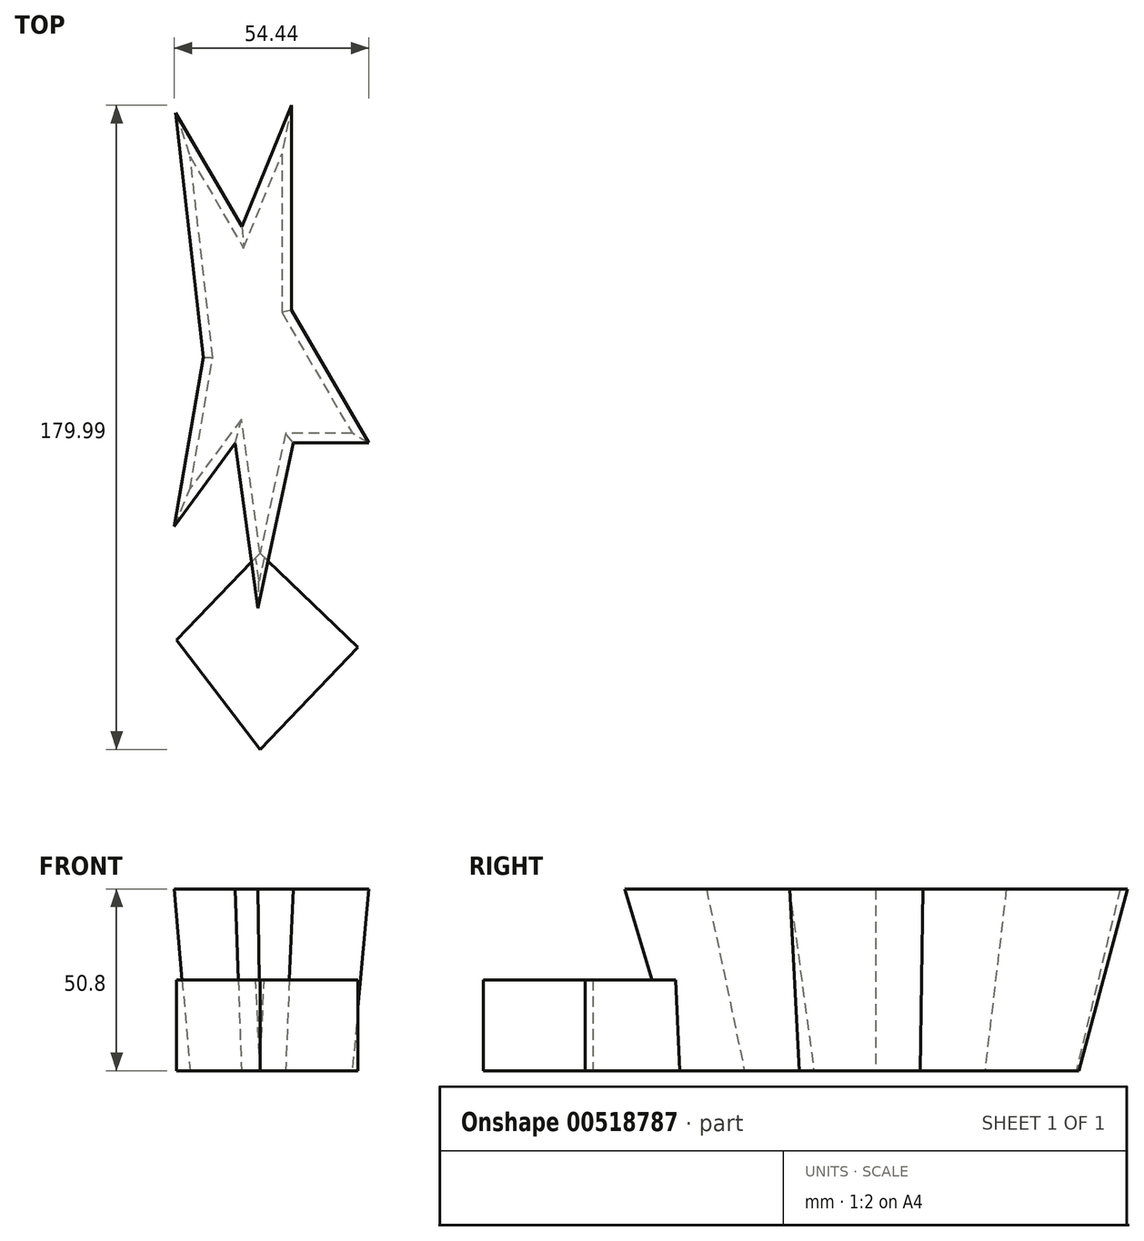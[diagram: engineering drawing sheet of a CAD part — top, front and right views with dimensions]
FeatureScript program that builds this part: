
annotation { "Feature Type Name" : "Feature", "Feature Type Description" : "" }
export const myFeature = defineFeature(function(context is Context, id is Id, definition is map)
    precondition{}
    {
        {
            var Q0;
            Q0=qCreatedBy(makeId("Top.planeOp"),FACE);
            var sketch = newSketch(context, id + "F0", { "sketchPlane" : qUnion([Q0])});
            skLineSegment(sketch, "E0", {"start": v(0, 0) * mm, "end": v(7.14, 33.47) * mm});
            skLineSegment(sketch, "E1", {"start": v(7.14, 33.47) * mm, "end": v(25.78, 33.47) * mm});
            skLineSegment(sketch, "E2", {"start": v(25.78, 33.47) * mm, "end": v(6.1, 67.24) * mm});
            skLineSegment(sketch, "E3", {"start": v(6.1, 67.24) * mm, "end": v(6.1, 111.57) * mm});
            skLineSegment(sketch, "E4", {"start": v(6.1, 111.57) * mm, "end": v(-4.61, 85.27) * mm});
            skLineSegment(sketch, "E5", {"start": v(-4.61, 85.27) * mm, "end": v(-19.5, 110.8) * mm});
            skLineSegment(sketch, "E6", {"start": v(-19.5, 110.8) * mm, "end": v(-13.2, 54.71) * mm});
            skLineSegment(sketch, "E7", {"start": v(-13.2, 54.71) * mm, "end": v(-19.5, 18.1) * mm});
            skLineSegment(sketch, "E8", {"start": v(-19.5, 18.1) * mm, "end": v(-5.2, 37.52) * mm});
            skLineSegment(sketch, "E9", {"start": v(-5.2, 37.52) * mm, "end": v(0, 0) * mm});
            skSolve(sketch);
        }
        {
            var Q0;
            Q0=makeQuery(id+"F0.imprint","IMPRINT",FACE,{"disambiguationData":[TD([[makeQuery(id+"F0.imprint","IMPRINT",EDGE,{"derivedFrom":sQuery(id+"F0.wireOp",EDGE,"E0")}),1.0]])]});
            extrude(context, id + "F1", {"entities" : qUnion([Q0]), "depth" : 50.8 * mm, "hasDraft" : true, "draftAngle" : 3 * degree});
        }
        {
            var Q0;
            Q0=qCreatedBy(makeId("Top.planeOp"),FACE);
            var sketch = newSketch(context, id + "F2", { "sketchPlane" : qUnion([Q0])});
            skLineSegment(sketch, "E10", {"start": v(0, 0) * mm, "end": v(27.38, -26.36) * mm});
            skLineSegment(sketch, "E11", {"start": v(27.38, -26.36) * mm, "end": v(0, -54.8) * mm});
            skLineSegment(sketch, "E12", {"start": v(0, -54.8) * mm, "end": v(50.11, -40.89) * mm});
            skLineSegment(sketch, "E13", {"start": v(50.11, -40.89) * mm, "end": v(40.59, -71) * mm});
            skLineSegment(sketch, "E14", {"start": v(40.59, -71) * mm, "end": v(82.99, -35.73) * mm});
            skLineSegment(sketch, "E15", {"start": v(82.99, -35.73) * mm, "end": v(117.82, -22.02) * mm});
            skLineSegment(sketch, "E16", {"start": v(117.82, -22.02) * mm, "end": v(97.28, 5.14) * mm});
            skLineSegment(sketch, "E17", {"start": v(97.28, 5.14) * mm, "end": v(106.73, 35) * mm});
            skLineSegment(sketch, "E18", {"start": v(106.73, 35) * mm, "end": v(67.32, 5.14) * mm});
            skLineSegment(sketch, "E19", {"start": v(67.32, 5.14) * mm, "end": v(57.62, 39.05) * mm});
            skLineSegment(sketch, "E20", {"start": v(57.62, 39.05) * mm, "end": v(45.27, 0) * mm});
            skLineSegment(sketch, "E21", {"start": v(45.27, 0) * mm, "end": v(0, 0) * mm});
            skLineSegment(sketch, "E22", {"start": v(0, 0) * mm, "end": v(-23.35, -24.26) * mm});
            skLineSegment(sketch, "E23", {"start": v(-23.35, -24.26) * mm, "end": v(0, -54.8) * mm});
            skLineSegment(sketch, "E24", {"start": v(0, -54.8) * mm, "end": v(-29.74, -54.8) * mm});
            skLineSegment(sketch, "E25", {"start": v(-29.74, -54.8) * mm, "end": v(-29.74, -76.29) * mm});
            skLineSegment(sketch, "E26", {"start": v(-29.74, -76.29) * mm, "end": v(-47.93, -58.78) * mm});
            skLineSegment(sketch, "E27", {"start": v(-47.93, -58.78) * mm, "end": v(-73.23, -71) * mm});
            skLineSegment(sketch, "E28", {"start": v(-73.23, -71) * mm, "end": v(-57.23, -51.4) * mm});
            skLineSegment(sketch, "E29", {"start": v(-57.23, -51.4) * mm, "end": v(-82.46, -51.4) * mm});
            skLineSegment(sketch, "E30", {"start": v(-82.46, -51.4) * mm, "end": v(-61.8, -35.73) * mm});
            skLineSegment(sketch, "E31", {"start": v(-61.8, -35.73) * mm, "end": v(-67.46, -15.9) * mm});
            skLineSegment(sketch, "E32", {"start": v(-67.46, -15.9) * mm, "end": v(-46.86, -35.73) * mm});
            skLineSegment(sketch, "E33", {"start": v(-46.86, -35.73) * mm, "end": v(-34.43, -6.34) * mm});
            skLineSegment(sketch, "E34", {"start": v(-34.43, -6.34) * mm, "end": v(-34.43, -35.73) * mm});
            skLineSegment(sketch, "E35", {"start": v(-34.43, -35.73) * mm, "end": v(0, -54.8) * mm});
            skSolve(sketch);
        }
        {
            var Q0;
            Q0=makeQuery(id+"F2.imprint","IMPRINT",FACE,{"disambiguationData":[TD([[makeQuery(id+"F2.imprint","IMPRINT",EDGE,{"derivedFrom":sQuery(id+"F2.wireOp",EDGE,"E10")}),-1.0]])]});
            extrude(context, id + "F3", {"entities" : qUnion([Q0]), "operationType" : NewBodyOperationType.ADD, "depth" : 25.4 * mm});
        }
    });
